# Revit family: 13324CHN
name_source: partatom
category: Plumbing Fixtures
units: mm (PartAtom-declared; Revit-internal decimal feet)

## family parameters
Always vertical = No
Cut with Voids When Loaded = No
OmniClass Number = 23.31.17.00
OmniClass Title = Showers
Part Type = Normal
Room Calculation Point = No
Round Connector Dimension = Use Diameter
Shared = No
Work Plane-Based = Yes

## types (2) — shared parameters
Connector Description = Water Inlet 12.7mm
Default Elevation = 1219 mm
Description = Ecostat Fine Shower thermostat for exposed installation
Diameter = 13 mm
Manufacturer = Hansgrohe
Model = 13324CHN
Product Guid = da28e6b4-0b84-409b-9118-a1cba73c5871
Product Page URL = https://www.hansgrohe.com
Product data url = https://bimobject.com
URL = https://www.hansgrohe.com
Version = 1

## per-type parameters (varying)
| type | Material |
| 007 Chrome | Hansgrohe - Metal - 007 Chrome |
| 677 Matte Black | Hansgrohe - Metal - 677 Matte Black |

## geometry (parser evidence)
native form markers: Sweep x3
no freeform markers — native parametric forms only
